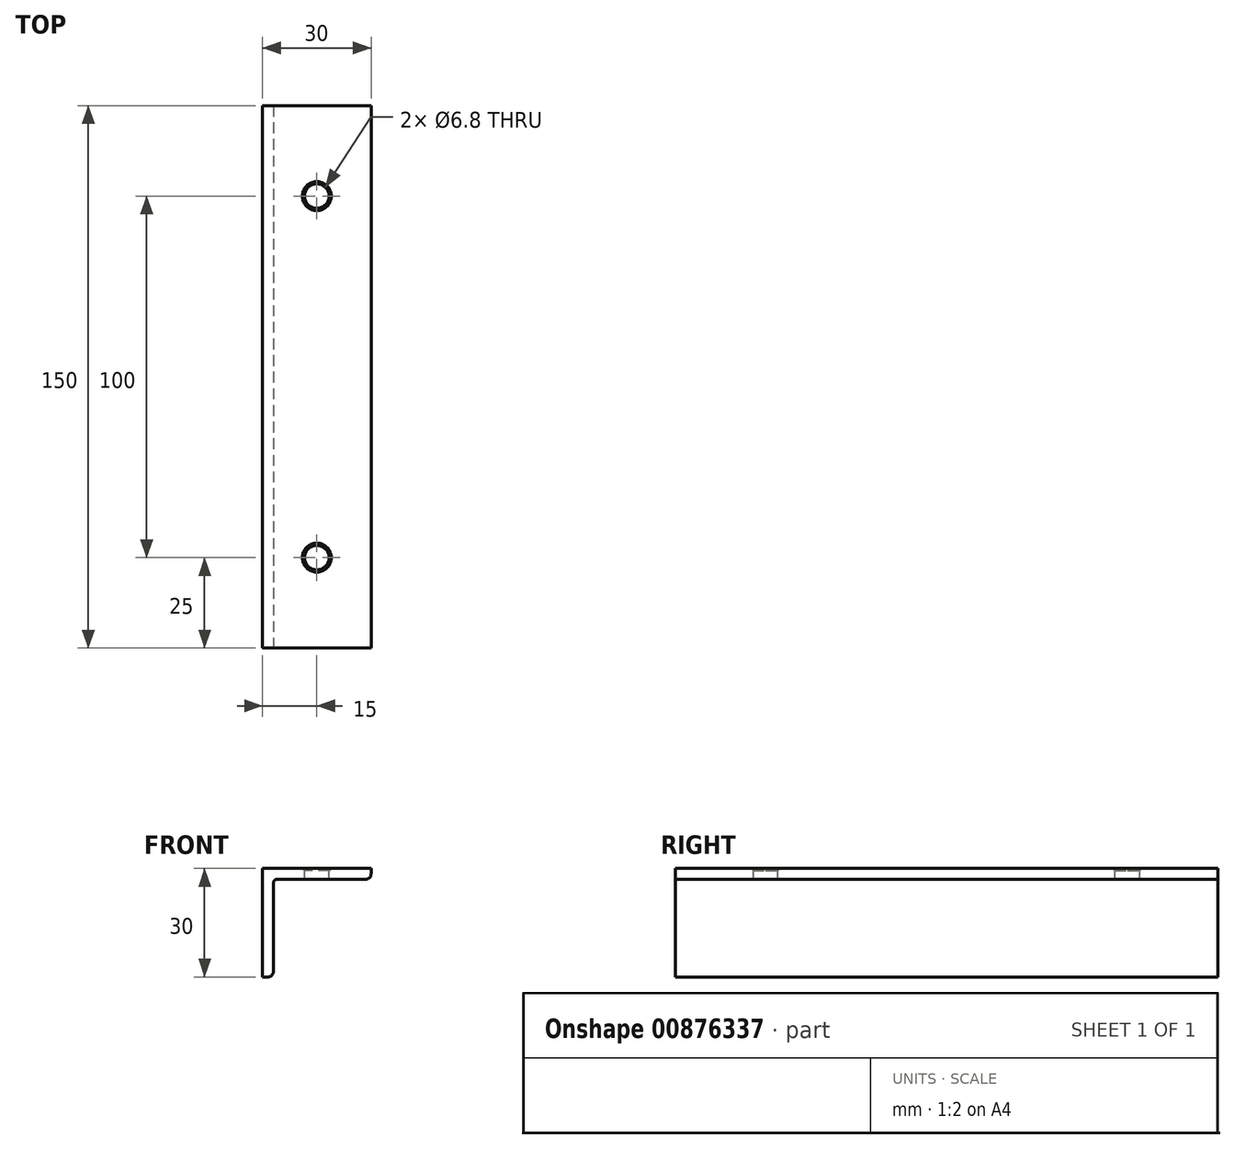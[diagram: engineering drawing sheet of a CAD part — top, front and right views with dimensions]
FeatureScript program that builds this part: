
annotation { "Feature Type Name" : "Feature", "Feature Type Description" : "" }
export const myFeature = defineFeature(function(context is Context, id is Id, definition is map)
    precondition{}
    {
        {
            var Q0;
            Q0=qCreatedBy(makeId("Front.planeOp"),FACE);
            var sketch = newSketch(context, id + "F0", { "sketchPlane" : qUnion([Q0])});
            skLineSegment(sketch, "E0", {"start": v(0, 0) * mm, "end": v(30, 0) * mm});
            skLineSegment(sketch, "E1", {"start": v(30, 0) * mm, "end": v(30, -1.5) * mm});
            skLineSegment(sketch, "E2", {"start": v(28.5, -3) * mm, "end": v(4, -3) * mm});
            skLineSegment(sketch, "E3", {"start": v(3, -4) * mm, "end": v(3, -28.5) * mm});
            skLineSegment(sketch, "E4", {"start": v(1.5, -30) * mm, "end": v(0, -30) * mm});
            skLineSegment(sketch, "E5", {"start": v(0, -30) * mm, "end": v(0, 0) * mm});
            skPoint(sketch, "E6.visualSharp", {"position": v(30, -3) * mm});
            skArc(sketch, "E6.filletArc", {"start": v(28.5, -3) * mm, "mid": v(29.56, -2.56) * mm, "end": v(30, -1.5) * mm});
            skPoint(sketch, "E7.visualSharp", {"position": v(3, -30) * mm});
            skArc(sketch, "E7.filletArc", {"start": v(1.5, -30) * mm, "mid": v(2.56, -29.56) * mm, "end": v(3, -28.5) * mm});
            skPoint(sketch, "E8.visualSharp", {"position": v(3, -3) * mm});
            skArc(sketch, "E8.filletArc", {"start": v(4, -3) * mm, "mid": v(3.3, -3.3) * mm, "end": v(3, -4) * mm});
            skSolve(sketch);
        }
        {
            var Q0;
            Q0=qCreatedBy(makeId("Right.planeOp"),FACE);
            var sketch = newSketch(context, id + "F1", { "sketchPlane" : qUnion([Q0])});
            skLineSegment(sketch, "E9", {"start": v(0, 0) * mm, "end": v(-150, 0) * mm});
            skSolve(sketch);
        }
        {
            var Q0;
            Q0=makeQuery(id+"F0.imprint","IMPRINT",FACE,{"disambiguationData":[TD([[makeQuery(id+"F0.imprint","IMPRINT",EDGE,{"derivedFrom":sQuery(id+"F0.wireOp",EDGE,"E0")}),-1.0]])]});
            var Q1;
            Q1=sQuery(id+"F1.wireOp",EDGE,"E9");
            sweep(context, id + "F2", {"profiles" : qUnion([Q0]), "path" : qUnion([Q1])});
        }
        {
            var Q0;
            Q0=qCreatedBy(makeId("Top.planeOp"),FACE);
            var sketch = newSketch(context, id + "F3", { "sketchPlane" : qUnion([Q0])});
            skCircle(sketch, "E10", {"center": v(15, -25) * mm, "radius": 4.5 * mm});
            skCircle(sketch, "E11", {"center": v(15, -125) * mm, "radius": 4.5 * mm});
            skCircle(sketch, "E12", {"center": v(15, -100) * mm, "radius": 4.5 * mm});
            skCircle(sketch, "E13", {"center": v(15, -50) * mm, "radius": 4.5 * mm});
            skSolve(sketch);
        }
        {
            var Q0;
            Q0=sQuery(id+"F3.wireOp",VERTEX,"E11.center");
            var Q1;
            Q1=sQuery(id+"F3.wireOp",VERTEX,"E10.center");
            var Q2;
            Q2=makeQuery(id+"F2.opSweep","SWEPT_BODY",BODY,{"disambiguationData":[OSD([sQuery(id+"F0.wireOp",EDGE,"E0"),sQuery(id+"F0.wireOp",EDGE,"E1"),sQuery(id+"F0.wireOp",EDGE,"E2"),sQuery(id+"F0.wireOp",EDGE,"E3"),sQuery(id+"F0.wireOp",EDGE,"E4"),sQuery(id+"F0.wireOp",EDGE,"E5"),sQuery(id+"F0.wireOp",EDGE,"E6.filletArc"),sQuery(id+"F0.wireOp",EDGE,"E7.filletArc"),sQuery(id+"F0.wireOp",EDGE,"E8.filletArc"),sQuery(id+"F1.wireOp",EDGE,"E9")])]});
            hole(context, id + "F4", {"style" : HoleStyle.C_SINK, "endStyle" : HoleEndStyle.BLIND, "holeDiameter" : 6.8 * mm, "cSinkDiameter" : 8 * mm, "cSinkAngle" : 90 * degree, "majorDiameter" : 8 * mm, "holeDepth" : 5 * mm, "isTappedThrough" : true, "tappedDepth" : 4 * mm, "tapClearance" : 0, "locations" : qUnion([Q0, Q1]), "scope" : qUnion([Q2])});
        }
    });
